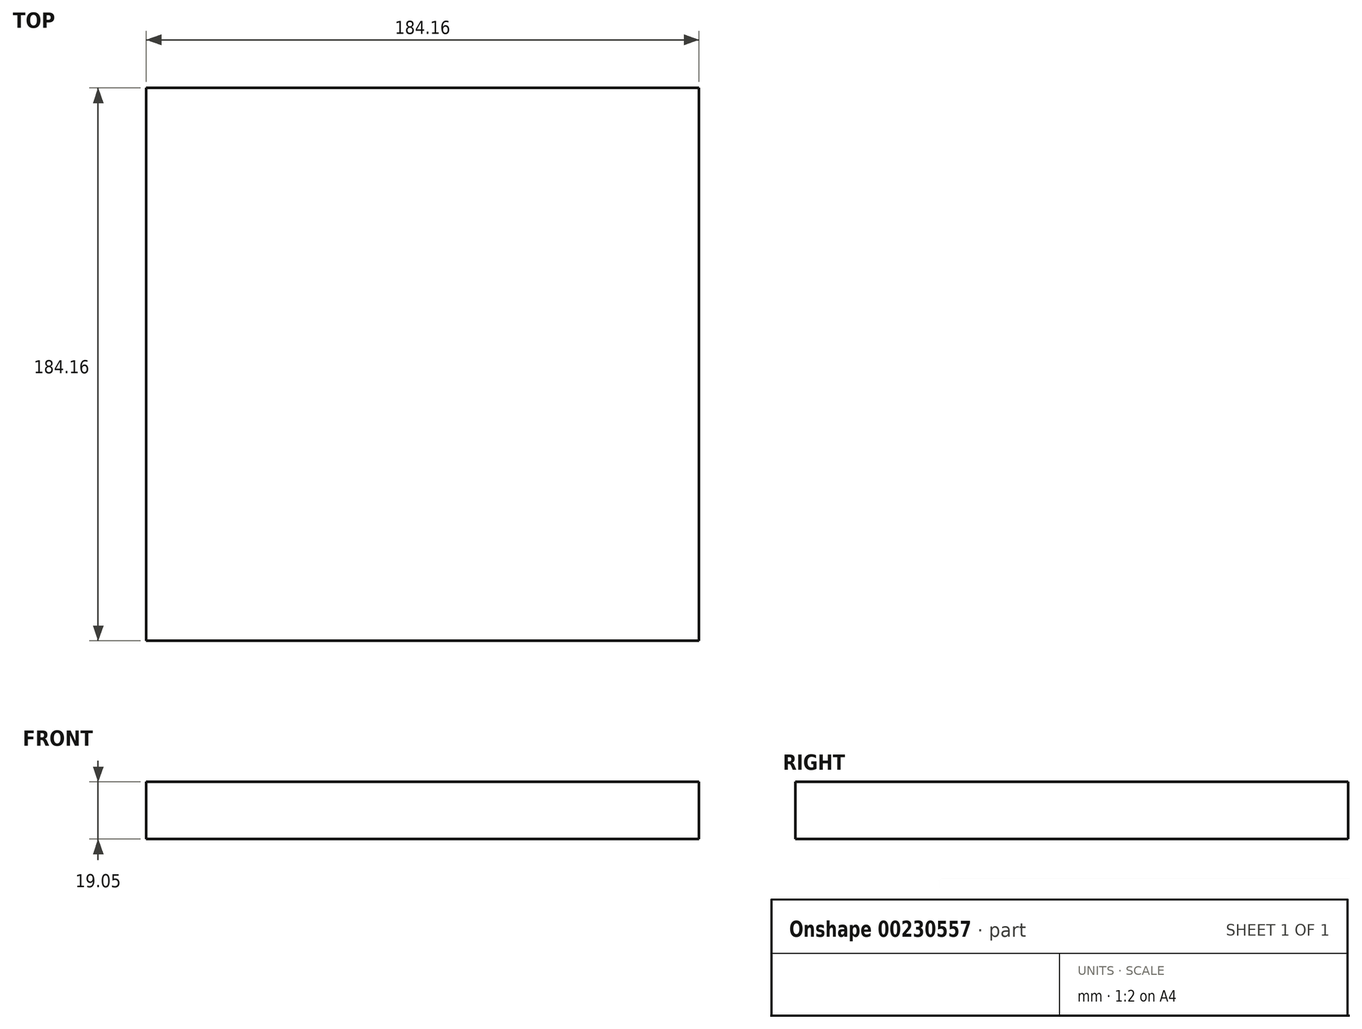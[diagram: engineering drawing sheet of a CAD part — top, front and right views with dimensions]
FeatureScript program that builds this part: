
annotation { "Feature Type Name" : "Feature", "Feature Type Description" : "" }
export const myFeature = defineFeature(function(context is Context, id is Id, definition is map)
    precondition{}
    {
        {
            var Q0;
            Q0=qCreatedBy(makeId("Top.planeOp"),FACE);
            var sketch = newSketch(context, id + "F0", { "sketchPlane" : qUnion([Q0])});
            skLineSegment(sketch, "E0.bottom", {"start": v(92.08, 92.08) * mm, "end": v(-92.07, 92.08) * mm});
            skLineSegment(sketch, "E0.top", {"start": v(92.08, -92.08) * mm, "end": v(-92.08, -92.08) * mm});
            skLineSegment(sketch, "E0.left", {"start": v(92.08, 92.08) * mm, "end": v(92.08, -92.08) * mm});
            skLineSegment(sketch, "E0.right", {"start": v(-92.07, 92.08) * mm, "end": v(-92.08, -92.08) * mm});
            skPoint(sketch, "E0.middle", {"position": v(0, 0) * mm});
            skSolve(sketch);
        }
        {
            var Q0;
            Q0=makeQuery(id+"F0.imprint","IMPRINT",FACE,{"disambiguationData":[TD([[makeQuery(id+"F0.imprint","IMPRINT",EDGE,{"derivedFrom":sQuery(id+"F0.wireOp",EDGE,"E0.bottom")}),1.0]])]});
            extrude(context, id + "F1", {"entities" : qUnion([Q0]), "depth" : 19.05 * mm});
        }
    });
